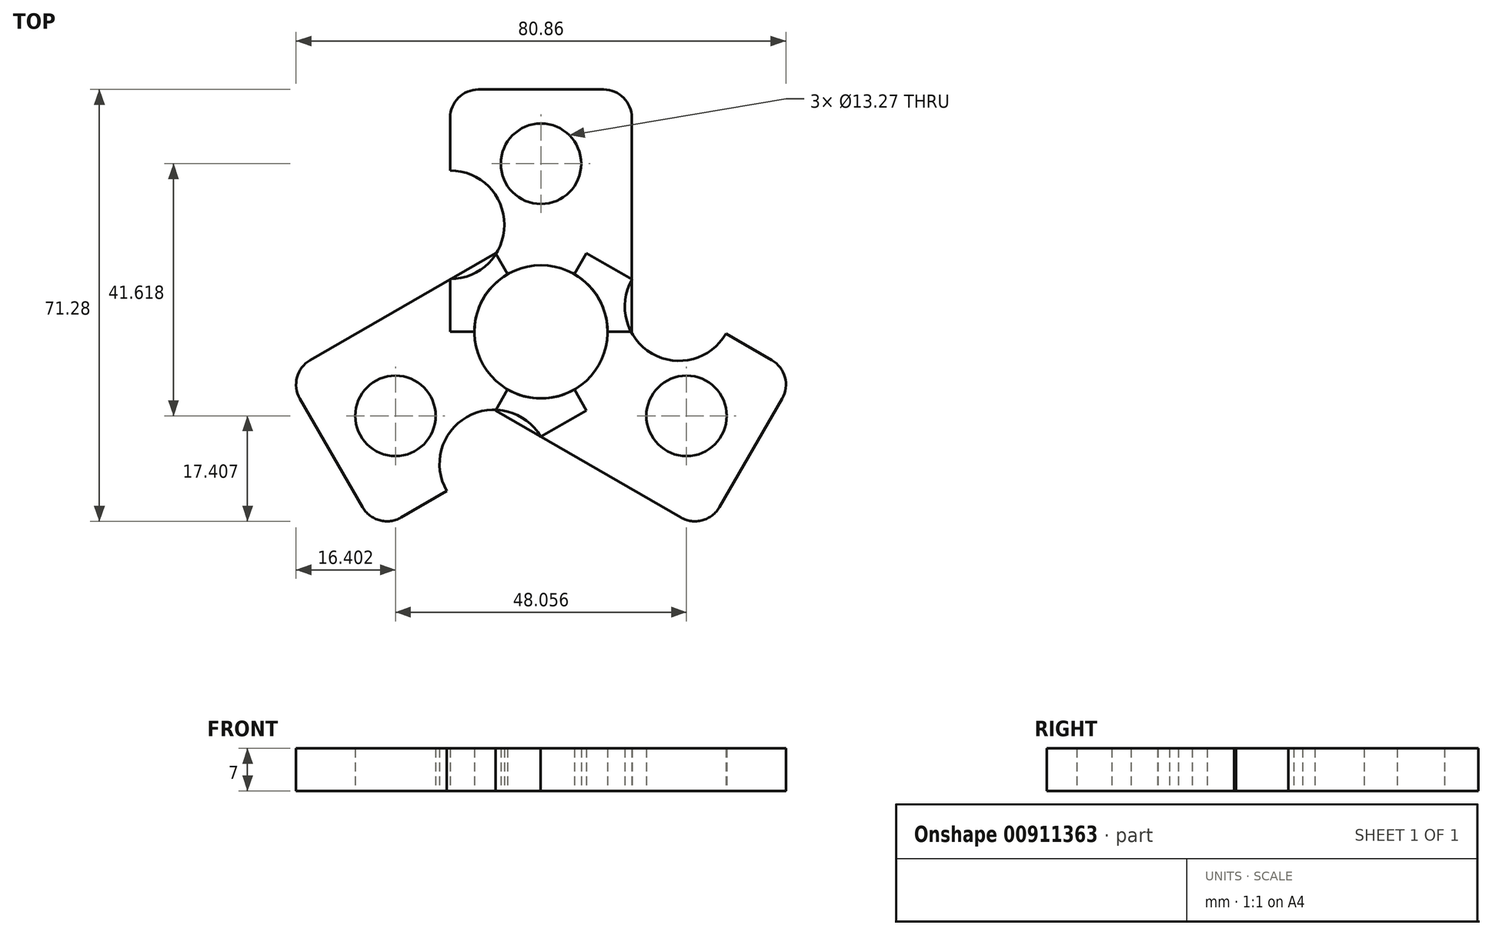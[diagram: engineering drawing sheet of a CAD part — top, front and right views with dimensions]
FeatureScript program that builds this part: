
annotation { "Feature Type Name" : "Feature", "Feature Type Description" : "" }
export const myFeature = defineFeature(function(context is Context, id is Id, definition is map)
    precondition{}
    {
        {
            var Q0;
            Q0=qCreatedBy(makeId("Top.planeOp"),FACE);
            var sketch = newSketch(context, id + "F0", { "sketchPlane" : qUnion([Q0])});
            skCircle(sketch, "E0", {"center": v(0, 0) * mm, "radius": 11 * mm});
            skLineSegment(sketch, "E1.bottom", {"start": v(0, 0) * mm, "end": v(15, 0) * mm});
            skLineSegment(sketch, "E1.top", {"start": v(0, 40) * mm, "end": v(10.33, 40) * mm});
            skLineSegment(sketch, "E1.left", {"start": v(0, 0) * mm, "end": v(0, 40) * mm});
            skLineSegment(sketch, "E1.right", {"start": v(15, 0) * mm, "end": v(15, 35.33) * mm});
            skLineSegment(sketch, "E2.bottom", {"start": v(0, 0) * mm, "end": v(-15, 0) * mm});
            skLineSegment(sketch, "E2.top", {"start": v(0, 40) * mm, "end": v(-10.33, 40) * mm});
            skLineSegment(sketch, "E2.right", {"start": v(-15, 0) * mm, "end": v(-15, 35.33) * mm});
            skLineSegment(sketch, "E3", {"start": v(0, 40) * mm, "end": v(0, 11) * mm});
            skLineSegment(sketch, "E4", {"start": v(0, 40) * mm, "end": v(0, 27.75) * mm});
            skCircle(sketch, "E5", {"center": v(0, 27.75) * mm, "radius": 6.64 * mm});
            skCircle(sketch, "E6", {"center": v(-15, 17.66) * mm, "radius": 8.95 * mm});
            skPoint(sketch, "E7.visualSharp", {"position": v(-15, 40) * mm});
            skArc(sketch, "E7.filletArc", {"start": v(-10.33, 40) * mm, "mid": v(-13.63, 38.63) * mm, "end": v(-15, 35.33) * mm});
            skPoint(sketch, "E8.visualSharp", {"position": v(15, 40) * mm});
            skArc(sketch, "E8.filletArc", {"start": v(15, 35.33) * mm, "mid": v(13.63, 38.63) * mm, "end": v(10.33, 40) * mm});
            skCircle(sketch, "E9.cCircle", {"center": v(-263.61, -11.4) * mm, "radius": 88.77 * mm, "construction": true});
            skLineSegment(sketch, "E9.0", {"start": v(-179.72, 47.51) * mm, "end": v(-170.66, -54.59) * mm});
            skLineSegment(sketch, "E9.1", {"start": v(-170.66, -54.59) * mm, "end": v(-254.55, -113.5) * mm});
            skLineSegment(sketch, "E9.2", {"start": v(-254.55, -113.5) * mm, "end": v(-347.5, -70.3) * mm});
            skLineSegment(sketch, "E9.3", {"start": v(-347.5, -70.3) * mm, "end": v(-356.57, 31.8) * mm});
            skLineSegment(sketch, "E9.4", {"start": v(-356.57, 31.8) * mm, "end": v(-272.68, 90.71) * mm});
            skLineSegment(sketch, "E9.5", {"start": v(-272.68, 90.71) * mm, "end": v(-179.72, 47.51) * mm});
            skPoint(sketch, "E9.0.midPoint", {"position": v(-175.2, -3.54) * mm});
            skSolve(sketch);
        }
        {
            var Q0;
            {var subQ0=sQuery(id+"F0.wireOp",EDGE,"E2.top");Q0=makeQuery(id+"F0.imprint","IMPRINT",FACE,{"disambiguationData":[TD([[makeQuery(id+"F0.imprint","IMPRINT",EDGE,{"derivedFrom":subQ0}),1.0]])]});}
            var Q1;
            {var subQ9=sQuery(id+"F0.wireOp",EDGE,"E1.top");Q1=makeQuery(id+"F0.imprint","IMPRINT",FACE,{"disambiguationData":[TD([[makeQuery(id+"F0.imprint","IMPRINT",EDGE,{"derivedFrom":subQ9}),-1.0]])]});}
            extrude(context, id + "F1", {"entities" : qUnion([Q0, Q1]), "depth" : 7 * mm, "offsetDistance" : 25 * mm});
        }
        {
            var Q0;
            Q0=qCreatedBy(makeId("Front.planeOp"),FACE);
            var sketch = newSketch(context, id + "F2", { "sketchPlane" : qUnion([Q0])});
            skLineSegment(sketch, "E10", {"start": v(0, -0.73) * mm, "end": v(0, 41.6) * mm});
            skSolve(sketch);
        }
        {
            var Q0;
            Q0=makeQuery(id+"F1.opExtrude","SWEPT_BODY",BODY,{"disambiguationData":[OSD([sQuery(id+"F0.wireOp",EDGE,"E0"),sQuery(id+"F0.wireOp",EDGE,"E1.bottom"),sQuery(id+"F0.wireOp",EDGE,"E1.top"),sQuery(id+"F0.wireOp",EDGE,"E1.right"),sQuery(id+"F0.wireOp",EDGE,"E2.bottom"),sQuery(id+"F0.wireOp",EDGE,"E2.top"),sQuery(id+"F0.wireOp",EDGE,"E2.right"),sQuery(id+"F0.wireOp",EDGE,"E5")])]});
            var Q1;
            Q1=sQuery(id+"F2.wireOp",EDGE,"E10");
            transform(context, id + "F3", {"entities" : qUnion([Q0]), "transformType" : TransformType.ROTATION, "transformAxis" : qUnion([Q1]), "angle" : 120 * degree, "makeCopy" : true});
        }
        {
            var Q0;
            Q0=makeQuery(id+"F1.opExtrude","SWEPT_BODY",BODY,{"disambiguationData":[OSD([sQuery(id+"F0.wireOp",EDGE,"E0"),sQuery(id+"F0.wireOp",EDGE,"E1.bottom"),sQuery(id+"F0.wireOp",EDGE,"E1.top"),sQuery(id+"F0.wireOp",EDGE,"E1.right"),sQuery(id+"F0.wireOp",EDGE,"E2.bottom"),sQuery(id+"F0.wireOp",EDGE,"E2.top"),sQuery(id+"F0.wireOp",EDGE,"E2.right"),sQuery(id+"F0.wireOp",EDGE,"E5")])]});
            var Q1;
            Q1=sQuery(id+"F2.wireOp",EDGE,"E10");
            transform(context, id + "F4", {"entities" : qUnion([Q0]), "transformType" : TransformType.ROTATION, "transformAxis" : qUnion([Q1]), "angle" : 240 * degree, "makeCopy" : true});
        }
    });
